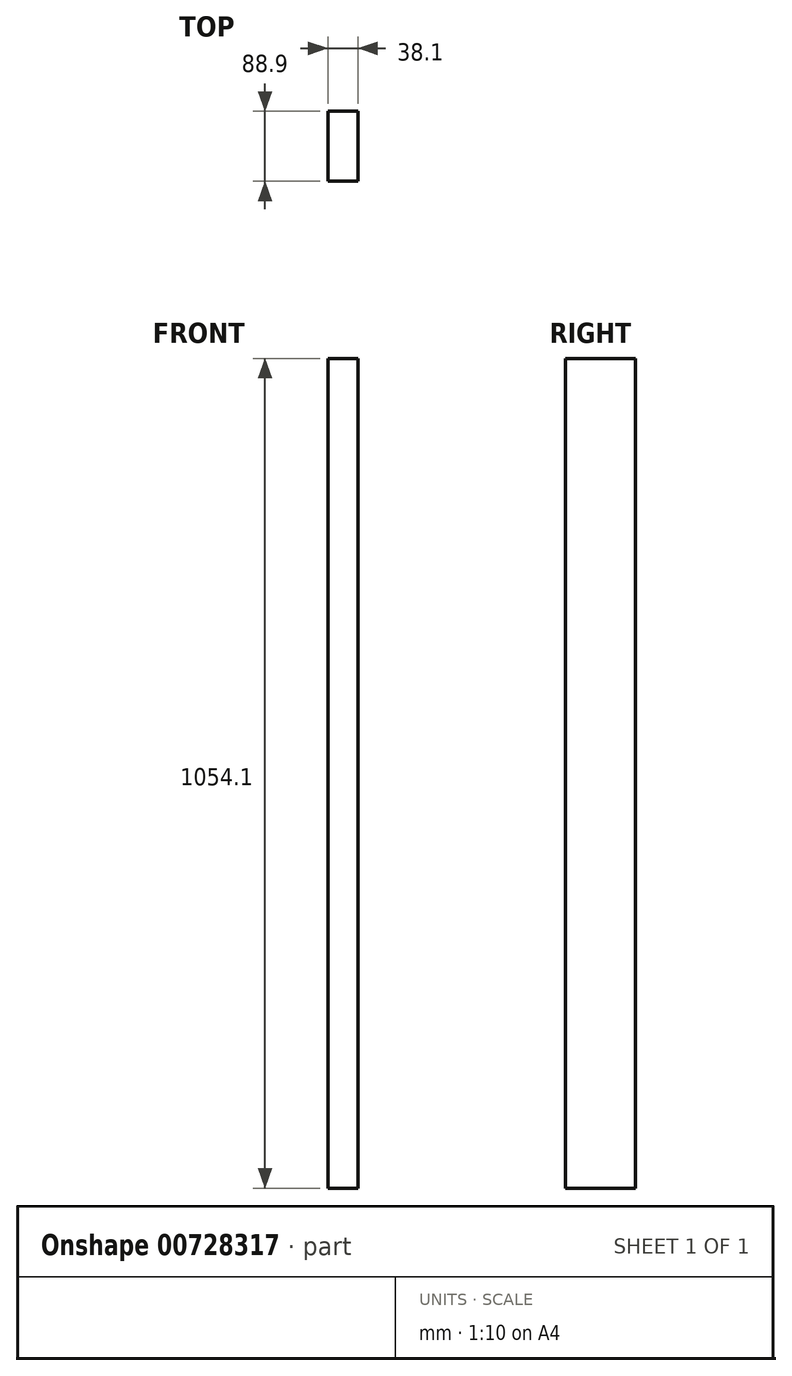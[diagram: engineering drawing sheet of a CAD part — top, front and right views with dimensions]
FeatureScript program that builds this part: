
annotation { "Feature Type Name" : "Feature", "Feature Type Description" : "" }
export const myFeature = defineFeature(function(context is Context, id is Id, definition is map)
    precondition{}
    {
        {
            var Q0;
            Q0=qCreatedBy(makeId("Front.planeOp"),FACE);
            var sketch = newSketch(context, id + "F0", { "sketchPlane" : qUnion([Q0])});
            skLineSegment(sketch, "E0.bottom", {"start": v(-19.05, -527.05) * mm, "end": v(19.05, -527.05) * mm});
            skLineSegment(sketch, "E0.top", {"start": v(-19.05, 527.05) * mm, "end": v(19.05, 527.05) * mm});
            skLineSegment(sketch, "E0.left", {"start": v(-19.05, -527.05) * mm, "end": v(-19.05, 527.05) * mm});
            skLineSegment(sketch, "E0.right", {"start": v(19.05, -527.05) * mm, "end": v(19.05, 527.05) * mm});
            skPoint(sketch, "E0.middle", {"position": v(0, 0) * mm});
            skSolve(sketch);
        }
        {
            var Q0;
            Q0=qSketchRegion(id+"F0",true);
            extrude(context, id + "F1", {"entities" : qUnion([Q0]), "depth" : 88.9 * mm});
        }
    });
